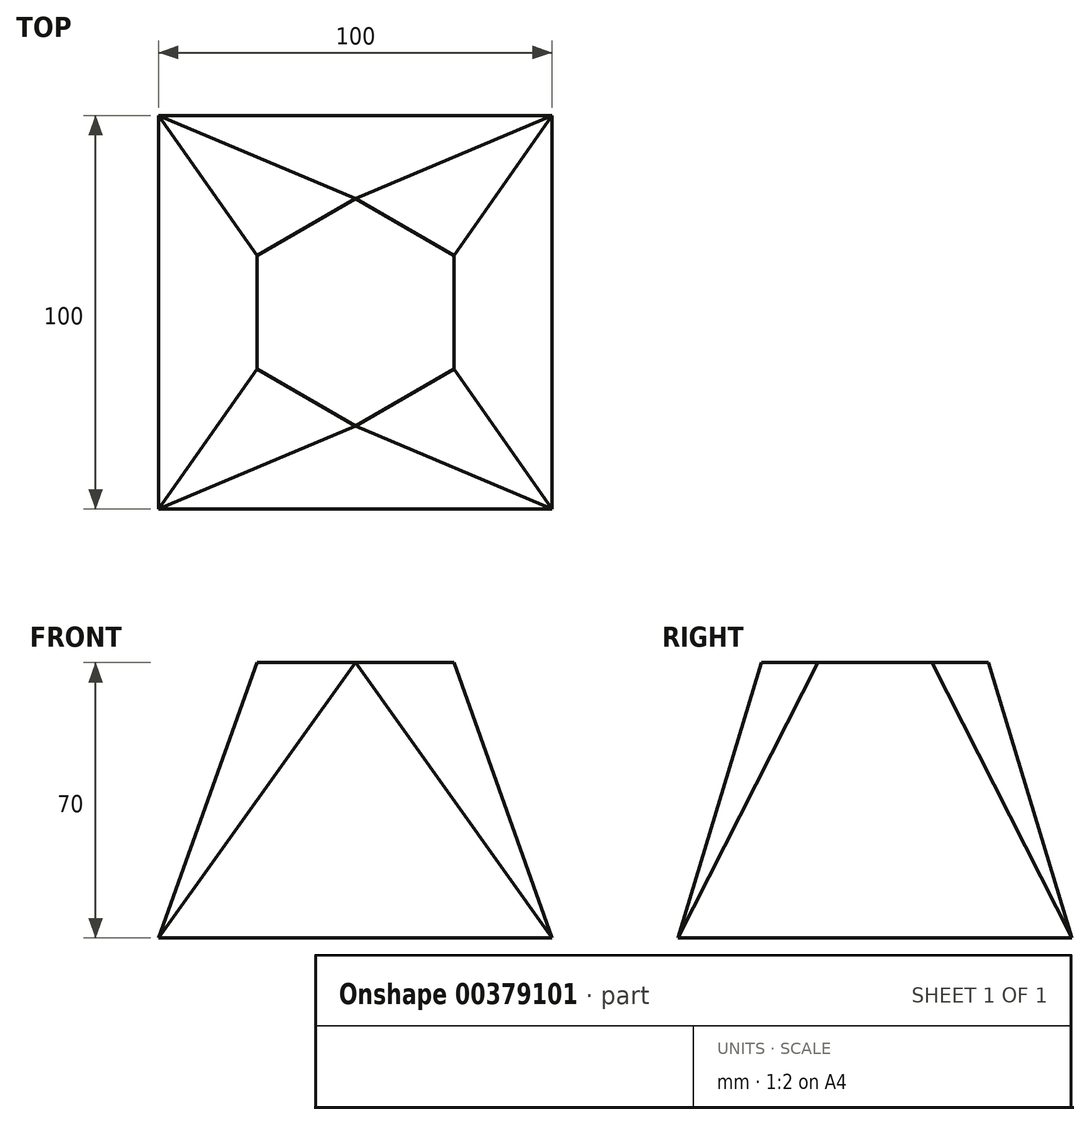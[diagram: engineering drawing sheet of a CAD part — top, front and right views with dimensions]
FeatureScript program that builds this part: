
annotation { "Feature Type Name" : "Feature", "Feature Type Description" : "" }
export const myFeature = defineFeature(function(context is Context, id is Id, definition is map)
    precondition{}
    {
        {
            var Q0;
            Q0=qCreatedBy(makeId("Top.planeOp"),FACE);
            var sketch = newSketch(context, id + "F0", { "sketchPlane" : qUnion([Q0])});
            skLineSegment(sketch, "E0.bottom", {"start": v(50, -50) * mm, "end": v(-50, -50) * mm});
            skLineSegment(sketch, "E0.top", {"start": v(50, 50) * mm, "end": v(-50, 50) * mm});
            skLineSegment(sketch, "E0.left", {"start": v(50, -50) * mm, "end": v(50, 50) * mm});
            skLineSegment(sketch, "E0.right", {"start": v(-50, -50) * mm, "end": v(-50, 50) * mm});
            skPoint(sketch, "E0.middle", {"position": v(0, 0) * mm});
            skSolve(sketch);
        }
        {
            var Q0;
            Q0=qCreatedBy(makeId("Top.planeOp"),FACE);
            cPlane(context, id + "F1", {"entities" : qUnion([Q0]), "cplaneType" : CPlaneType.OFFSET, "offset" : 70 * mm, "width" : 150 * mm, "height" : 150 * mm});
        }
        {
            var Q0;
            Q0=qCreatedBy(id+"F1.planeOp",FACE);
            var sketch = newSketch(context, id + "F2", { "sketchPlane" : qUnion([Q0])});
            skCircle(sketch, "E1.cCircle", {"center": v(0, 0) * mm, "radius": 28.87 * mm, "construction": true});
            skLineSegment(sketch, "E1.0", {"start": v(0, -28.87) * mm, "end": v(-25, -14.43) * mm});
            skLineSegment(sketch, "E1.1", {"start": v(-25, -14.43) * mm, "end": v(-25, 14.43) * mm});
            skLineSegment(sketch, "E1.2", {"start": v(-25, 14.43) * mm, "end": v(0, 28.87) * mm});
            skLineSegment(sketch, "E1.3", {"start": v(0, 28.87) * mm, "end": v(25, 14.43) * mm});
            skLineSegment(sketch, "E1.4", {"start": v(25, 14.43) * mm, "end": v(25, -14.43) * mm});
            skLineSegment(sketch, "E1.5", {"start": v(25, -14.43) * mm, "end": v(0, -28.87) * mm});
            skLineSegment(sketch, "E2.bottom", {"start": v(25, -28.87) * mm, "end": v(-25, -28.87) * mm});
            skLineSegment(sketch, "E2.top", {"start": v(25, 28.87) * mm, "end": v(-25, 28.87) * mm});
            skLineSegment(sketch, "E2.left", {"start": v(25, -28.87) * mm, "end": v(25, 28.87) * mm});
            skLineSegment(sketch, "E2.right", {"start": v(-25, -28.87) * mm, "end": v(-25, 28.87) * mm});
            skSolve(sketch);
        }
        {
            var Q0;
            {var subQ0=sQuery(id+"F2.wireOp",EDGE,"E1.0");Q0=makeQuery(id+"F2.imprint","IMPRINT",FACE,{"disambiguationData":[TD([[makeQuery(id+"F2.imprint","IMPRINT",EDGE,{"derivedFrom":subQ0}),1.0]])]});}
            var Q1;
            Q1=sQuery(id+"F0.wireOp",VERTEX,"E0.right.start");
            loft(context, id + "F3", {"sheetProfilesArray" : [{ "sheetProfileEntities" : qUnion([Q0]) }, { "sheetProfileEntities" : qUnion([Q1]) }]});
        }
        {
            var Q0;
            {var subQ0=sQuery(id+"F2.wireOp",EDGE,"E1.0");Q0=makeQuery(id+"F3.opLoft","SWEPT_BODY",BODY,{"disambiguationData":[OSD([sQuery(id+"F0.wireOp",VERTEX,"E0.right.start"),makeQuery(id+"F2.imprint","IMPRINT",FACE,{"disambiguationData":[TD([[makeQuery(id+"F2.imprint","IMPRINT",EDGE,{"derivedFrom":subQ0}),1.0]])]})])]});}
            var Q1;
            Q1=qCreatedBy(makeId("Front.planeOp"),FACE);
            mirror(context, id + "F4", {"entities" : qUnion([Q0]), "mirrorPlane" : qUnion([Q1])});
        }
        {
            var Q0;
            {var subQ0=sQuery(id+"F2.wireOp",EDGE,"E1.0");Q0=makeQuery(id+"F4.opPattern","COPY",BODY,{"derivedFrom":makeQuery(id+"F3.opLoft","SWEPT_BODY",BODY,{"disambiguationData":[OSD([sQuery(id+"F0.wireOp",VERTEX,"E0.right.start"),makeQuery(id+"F2.imprint","IMPRINT",FACE,{"disambiguationData":[TD([[makeQuery(id+"F2.imprint","IMPRINT",EDGE,{"derivedFrom":subQ0}),1.0]])]})])]}),"instanceName":"1"});}
            var Q1;
            {var subQ0=sQuery(id+"F2.wireOp",EDGE,"E1.0");Q1=makeQuery(id+"F3.opLoft","SWEPT_BODY",BODY,{"disambiguationData":[OSD([sQuery(id+"F0.wireOp",VERTEX,"E0.right.start"),makeQuery(id+"F2.imprint","IMPRINT",FACE,{"disambiguationData":[TD([[makeQuery(id+"F2.imprint","IMPRINT",EDGE,{"derivedFrom":subQ0}),1.0]])]})])]});}
            var Q2;
            Q2=qCreatedBy(makeId("Right.planeOp"),FACE);
            mirror(context, id + "F5", {"entities" : qUnion([Q0, Q1]), "mirrorPlane" : qUnion([Q2])});
        }
        {
            var Q0;
            Q0=qCreatedBy(id+"F1.planeOp",FACE);
            var sketch = newSketch(context, id + "F6", { "sketchPlane" : qUnion([Q0])});
            skLineSegment(sketch, "E3.bottom", {"start": v(25, -28.87) * mm, "end": v(-25, -28.87) * mm});
            skLineSegment(sketch, "E3.top", {"start": v(25, 28.87) * mm, "end": v(-25, 28.87) * mm});
            skLineSegment(sketch, "E3.left", {"start": v(25, -28.87) * mm, "end": v(25, 28.87) * mm});
            skLineSegment(sketch, "E3.right", {"start": v(-25, -28.87) * mm, "end": v(-25, 28.87) * mm});
            skPoint(sketch, "E3.middle", {"position": v(0, 0) * mm});
            skSolve(sketch);
        }
        {
            var Q0;
            Q0=makeQuery(id+"F0.imprint","IMPRINT",FACE,{"disambiguationData":[TD([[makeQuery(id+"F0.imprint","IMPRINT",EDGE,{"derivedFrom":sQuery(id+"F0.wireOp",EDGE,"E0.bottom")}),-1.0]])]});
            var Q1;
            Q1 = qSketchRegion(id + "F6", true);
            loft(context, id + "F7", {"sheetProfilesArray" : [{ "sheetProfileEntities" : qUnion([Q0]) }, { "sheetProfileEntities" : qUnion([Q1]) }]});
        }
        {
            var Q0;
            {var subQ0=sQuery(id+"F2.wireOp",EDGE,"E1.0");Q0=makeQuery(id+"F3.opLoft","SWEPT_BODY",BODY,{"disambiguationData":[OSD([sQuery(id+"F0.wireOp",VERTEX,"E0.right.start"),makeQuery(id+"F2.imprint","IMPRINT",FACE,{"disambiguationData":[TD([[makeQuery(id+"F2.imprint","IMPRINT",EDGE,{"derivedFrom":subQ0}),1.0]])]})])]});}
            var Q1;
            {var subQ0=sQuery(id+"F2.wireOp",EDGE,"E1.0");Q1=makeQuery(id+"F4.opPattern","COPY",BODY,{"derivedFrom":makeQuery(id+"F3.opLoft","SWEPT_BODY",BODY,{"disambiguationData":[OSD([sQuery(id+"F0.wireOp",VERTEX,"E0.right.start"),makeQuery(id+"F2.imprint","IMPRINT",FACE,{"disambiguationData":[TD([[makeQuery(id+"F2.imprint","IMPRINT",EDGE,{"derivedFrom":subQ0}),1.0]])]})])]}),"instanceName":"1"});}
            var Q2;
            {var subQ0=sQuery(id+"F2.wireOp",EDGE,"E1.0");Q2=makeQuery(id+"F5.opPattern","COPY",BODY,{"derivedFrom":makeQuery(id+"F3.opLoft","SWEPT_BODY",BODY,{"disambiguationData":[OSD([sQuery(id+"F0.wireOp",VERTEX,"E0.right.start"),makeQuery(id+"F2.imprint","IMPRINT",FACE,{"disambiguationData":[TD([[makeQuery(id+"F2.imprint","IMPRINT",EDGE,{"derivedFrom":subQ0}),1.0]])]})])]}),"instanceName":"1"});}
            var Q3;
            {var subQ0=sQuery(id+"F2.wireOp",EDGE,"E1.0");Q3=makeQuery(id+"F5.opPattern","COPY",BODY,{"derivedFrom":makeQuery(id+"F4.opPattern","COPY",BODY,{"derivedFrom":makeQuery(id+"F3.opLoft","SWEPT_BODY",BODY,{"disambiguationData":[OSD([sQuery(id+"F0.wireOp",VERTEX,"E0.right.start"),makeQuery(id+"F2.imprint","IMPRINT",FACE,{"disambiguationData":[TD([[makeQuery(id+"F2.imprint","IMPRINT",EDGE,{"derivedFrom":subQ0}),1.0]])]})])]}),"instanceName":"1"}),"instanceName":"1"});}
            var Q4;
            Q4=makeQuery(id+"F7.opLoft","SWEPT_BODY",BODY,{"disambiguationData":[OSD([makeQuery(id+"F0.imprint","IMPRINT",FACE,{"disambiguationData":[TD([[makeQuery(id+"F0.imprint","IMPRINT",EDGE,{"derivedFrom":sQuery(id+"F0.wireOp",EDGE,"E0.bottom")}),-1.0]])]}),makeQuery(id+"F6.imprint","IMPRINT",FACE,{"disambiguationData":[TD([[makeQuery(id+"F6.imprint","IMPRINT",EDGE,{"derivedFrom":sQuery(id+"F6.wireOp",EDGE,"E3.bottom")}),-1.0]])]})])]});
            booleanBodies(context, id + "F8", {"operationType" : BooleanOperationType.SUBTRACTION, "tools" : qUnion([Q0, Q1, Q2, Q3]), "targets" : qUnion([Q4])});
        }
    });
